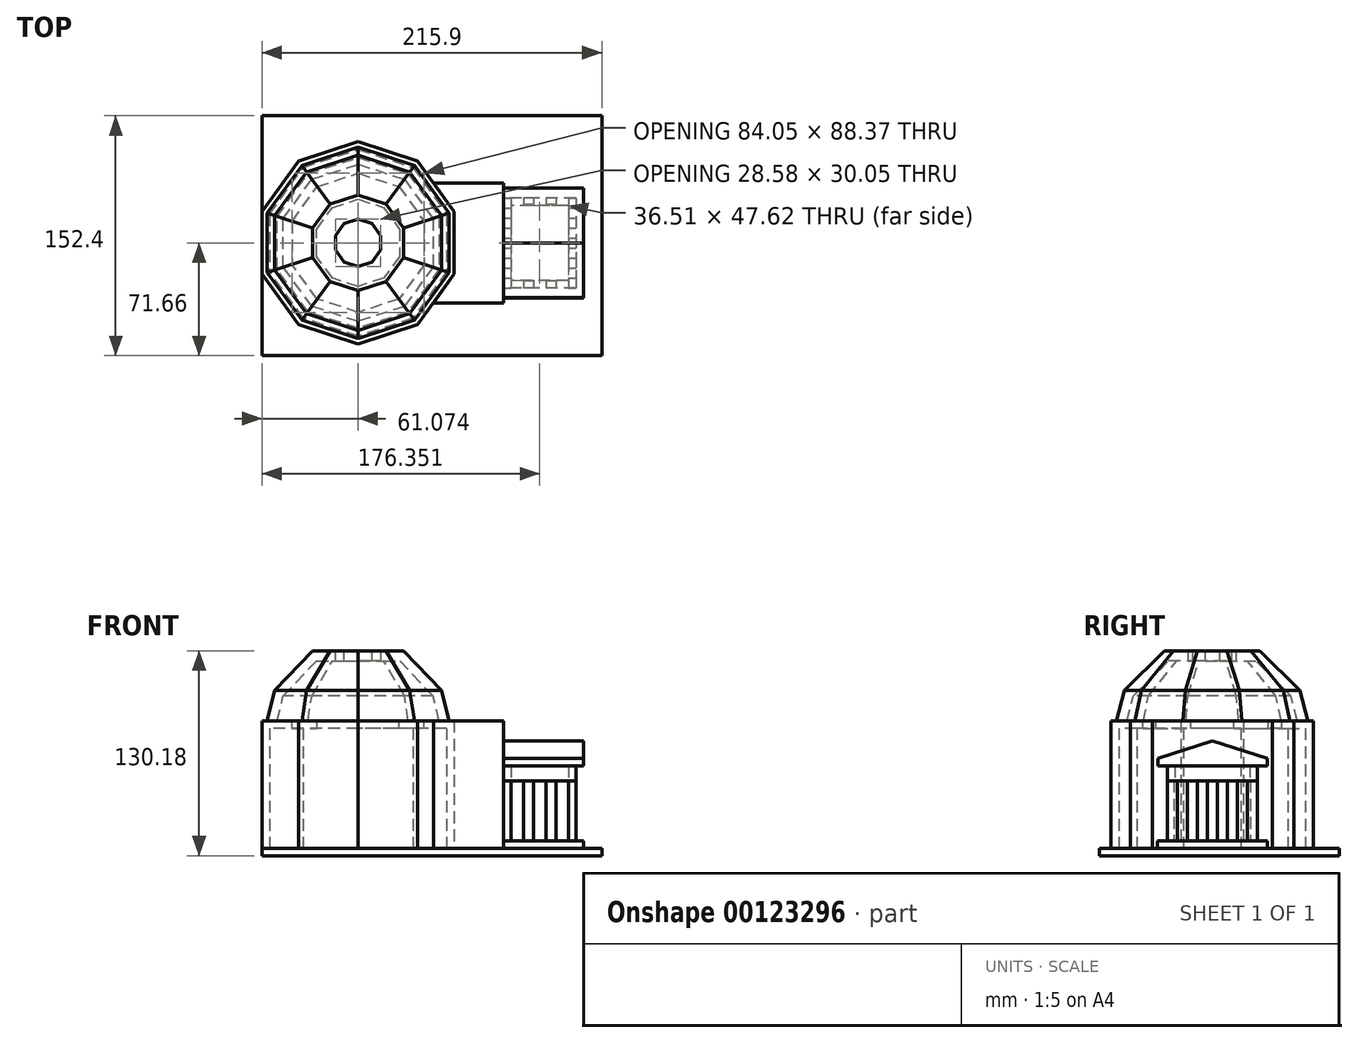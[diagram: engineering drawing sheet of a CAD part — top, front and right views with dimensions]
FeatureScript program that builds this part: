
annotation { "Feature Type Name" : "Feature", "Feature Type Description" : "" }
export const myFeature = defineFeature(function(context is Context, id is Id, definition is map)
    precondition{}
    {
        {
            var Q0;
            Q0=qCreatedBy(makeId("Top.planeOp"),FACE);
            var sketch = newSketch(context, id + "F0", { "sketchPlane" : qUnion([Q0])});
            skLineSegment(sketch, "E0.bottom", {"start": v(-108.2, 80.74) * mm, "end": v(107.7, 80.74) * mm});
            skLineSegment(sketch, "E0.top", {"start": v(-108.2, -71.66) * mm, "end": v(107.7, -71.66) * mm});
            skLineSegment(sketch, "E0.left", {"start": v(-108.2, 80.74) * mm, "end": v(-108.2, -71.66) * mm});
            skLineSegment(sketch, "E0.right", {"start": v(107.7, 80.74) * mm, "end": v(107.7, -71.66) * mm});
            skPoint(sketch, "E0.middle", {"position": v(-0.26, 4.54) * mm});
            skSolve(sketch);
        }
        {
            var Q0;
            Q0=qSketchRegion(id+"F0",true);
            extrude(context, id + "F1", {"entities" : qUnion([Q0]), "depth" : 4.76 * mm});
        }
        {
            var Q0;
            Q0=makeQuery(id+"F1.opExtrude","CAP_FACE",FACE,{"disambiguationData":[OSD([sQuery(id+"F0.wireOp",EDGE,"E0.bottom"),sQuery(id+"F0.wireOp",EDGE,"E0.top"),sQuery(id+"F0.wireOp",EDGE,"E0.left"),sQuery(id+"F0.wireOp",EDGE,"E0.right")])],"isStart":false});
            var sketch = newSketch(context, id + "F2", { "sketchPlane" : qUnion([Q0])});
            skCircle(sketch, "E1.cCircle", {"center": v(-47.14, 0) * mm, "radius": 61.07 * mm, "construction": true});
            skLineSegment(sketch, "E1.0", {"start": v(-47.14, 64.22) * mm, "end": v(-9.4, 51.95) * mm});
            skLineSegment(sketch, "E1.1", {"start": v(-9.4, 51.95) * mm, "end": v(13.94, 19.84) * mm});
            skLineSegment(sketch, "E1.2", {"start": v(13.94, 19.84) * mm, "end": v(13.94, -19.84) * mm});
            skLineSegment(sketch, "E1.3", {"start": v(13.94, -19.84) * mm, "end": v(-9.4, -51.95) * mm});
            skLineSegment(sketch, "E1.4", {"start": v(-9.4, -51.95) * mm, "end": v(-47.14, -64.22) * mm});
            skLineSegment(sketch, "E1.5", {"start": v(-47.14, -64.22) * mm, "end": v(-84.88, -51.95) * mm});
            skLineSegment(sketch, "E1.6", {"start": v(-84.88, -51.95) * mm, "end": v(-108.2, -19.84) * mm});
            skLineSegment(sketch, "E1.7", {"start": v(-108.2, -19.84) * mm, "end": v(-108.2, 19.84) * mm});
            skLineSegment(sketch, "E1.8", {"start": v(-108.2, 19.84) * mm, "end": v(-84.88, 51.95) * mm});
            skLineSegment(sketch, "E1.9", {"start": v(-84.88, 51.95) * mm, "end": v(-47.14, 64.22) * mm});
            skPoint(sketch, "E1.0.midPoint", {"position": v(-28.26, 58.08) * mm});
            skLineSegment(sketch, "E2", {"start": v(45.12, 0) * mm, "end": v(45.12, 38.1) * mm});
            skPoint(sketch, "E2.startSnap0", {"position": v(13.94, 0) * mm});
            skLineSegment(sketch, "E3", {"start": v(45.12, 0) * mm, "end": v(45.12, -38.1) * mm});
            skLineSegment(sketch, "E4", {"start": v(45.12, 38.1) * mm, "end": v(0.67, 38.1) * mm});
            skLineSegment(sketch, "E5", {"start": v(45.12, -38.1) * mm, "end": v(0.67, -38.1) * mm});
            skSolve(sketch);
        }
        {
            var Q0;
            {var subQ2=sQuery(id+"F2.wireOp",EDGE,"E1.0");Q0=makeQuery(id+"F2.imprint","IMPRINT",FACE,{"disambiguationData":[TD([[makeQuery(id+"F2.imprint","IMPRINT",EDGE,{"derivedFrom":subQ2}),-1.0]])]});}
            extrude(context, id + "F3", {"entities" : qUnion([Q0]), "depth" : 80.96 * mm});
        }
        {
            var Q0;
            Q0=makeQuery(id+"F3.opExtrude","CAP_FACE",FACE,{"disambiguationData":[OSD([sQuery(id+"F2.wireOp",EDGE,"E1.0"),sQuery(id+"F2.wireOp",EDGE,"E1.1"),sQuery(id+"F2.wireOp",EDGE,"E1.2"),sQuery(id+"F2.wireOp",EDGE,"E1.3"),sQuery(id+"F2.wireOp",EDGE,"E1.4"),sQuery(id+"F2.wireOp",EDGE,"E1.5"),sQuery(id+"F2.wireOp",EDGE,"E1.6"),sQuery(id+"F2.wireOp",EDGE,"E1.7"),sQuery(id+"F2.wireOp",EDGE,"E1.8"),sQuery(id+"F2.wireOp",EDGE,"E1.9")])],"isStart":true});
            shell(context, id + "F4", {"entities" : qUnion([Q0]), "thickness" : 4.76 * mm});
        }
        {
            var Q0;
            Q0=makeQuery(id+"F3.opExtrude","CAP_FACE",FACE,{"disambiguationData":[OSD([sQuery(id+"F2.wireOp",EDGE,"E1.0"),sQuery(id+"F2.wireOp",EDGE,"E1.1"),sQuery(id+"F2.wireOp",EDGE,"E1.2"),sQuery(id+"F2.wireOp",EDGE,"E1.3"),sQuery(id+"F2.wireOp",EDGE,"E1.4"),sQuery(id+"F2.wireOp",EDGE,"E1.5"),sQuery(id+"F2.wireOp",EDGE,"E1.6"),sQuery(id+"F2.wireOp",EDGE,"E1.7"),sQuery(id+"F2.wireOp",EDGE,"E1.8"),sQuery(id+"F2.wireOp",EDGE,"E1.9")])],"isStart":false});
            var sketch = newSketch(context, id + "F5", { "sketchPlane" : qUnion([Q0])});
            skLineSegment(sketch, "E6.0", {"start": v(-89.16, 13.65) * mm, "end": v(-73.1, 35.75) * mm});
            skLineSegment(sketch, "E6.1", {"start": v(-73.1, 35.75) * mm, "end": v(-47.14, 44.19) * mm});
            skLineSegment(sketch, "E6.2", {"start": v(-89.16, 13.65) * mm, "end": v(-89.16, -13.65) * mm});
            skLineSegment(sketch, "E6.3", {"start": v(-47.14, 44.19) * mm, "end": v(-21.16, 35.75) * mm});
            skLineSegment(sketch, "E6.4", {"start": v(-21.16, 35.75) * mm, "end": v(-5.11, 13.65) * mm});
            skLineSegment(sketch, "E6.5", {"start": v(-5.11, 13.65) * mm, "end": v(-5.11, -13.65) * mm});
            skLineSegment(sketch, "E6.6", {"start": v(-73.1, -35.75) * mm, "end": v(-89.16, -13.65) * mm});
            skLineSegment(sketch, "E6.7", {"start": v(-47.14, -44.19) * mm, "end": v(-73.1, -35.75) * mm});
            skLineSegment(sketch, "E6.8", {"start": v(-21.16, -35.75) * mm, "end": v(-47.14, -44.19) * mm});
            skLineSegment(sketch, "E6.9", {"start": v(-5.11, -13.65) * mm, "end": v(-21.16, -35.75) * mm});
            skSolve(sketch);
        }
        {
            var Q0;
            Q0=qSketchRegion(id+"F5",true);
            extrude(context, id + "F6", {"entities" : qUnion([Q0]), "operationType" : NewBodyOperationType.REMOVE, "oppositeDirection" : true, "depth" : 25.4 * mm});
        }
        {
            var Q0;
            {var subQ1=sQuery(id+"F2.wireOp",EDGE,"E1.2");Q0=makeQuery(id+"F2.imprint","IMPRINT",FACE,{"disambiguationData":[TD([[makeQuery(id+"F2.imprint","IMPRINT",EDGE,{"derivedFrom":subQ1}),1.0]])]});}
            var Q1;
            Q1=makeQuery(id+"F3.opExtrude","CAP_FACE",FACE,{"disambiguationData":[OSD([sQuery(id+"F2.wireOp",EDGE,"E1.0"),sQuery(id+"F2.wireOp",EDGE,"E1.1"),sQuery(id+"F2.wireOp",EDGE,"E1.2"),sQuery(id+"F2.wireOp",EDGE,"E1.3"),sQuery(id+"F2.wireOp",EDGE,"E1.4"),sQuery(id+"F2.wireOp",EDGE,"E1.5"),sQuery(id+"F2.wireOp",EDGE,"E1.6"),sQuery(id+"F2.wireOp",EDGE,"E1.7"),sQuery(id+"F2.wireOp",EDGE,"E1.8"),sQuery(id+"F2.wireOp",EDGE,"E1.9")])],"isStart":false});
            extrude(context, id + "F7", {"entities" : qUnion([Q0]), "endBound" : BoundingType.UP_TO_SURFACE, "endBoundEntityFace" : qUnion([Q1]), "depth" : 25.4 * mm});
        }
        {
            var Q0;
            {var subQ2=sQuery(id+"F2.wireOp",EDGE,"E1.0");Q0=makeQuery(id+"F2.imprint","IMPRINT",FACE,{"disambiguationData":[TD([[makeQuery(id+"F2.imprint","IMPRINT",EDGE,{"derivedFrom":subQ2}),1.0]])]});}
            var sketch = newSketch(context, id + "F8", { "sketchPlane" : qUnion([Q0])});
            skLineSegment(sketch, "E7.bottom", {"start": v(45.12, 34.93) * mm, "end": v(95.92, 34.93) * mm});
            skLineSegment(sketch, "E7.top", {"start": v(45.12, -34.92) * mm, "end": v(95.92, -34.92) * mm});
            skLineSegment(sketch, "E7.left", {"start": v(45.12, 34.93) * mm, "end": v(45.12, -34.93) * mm});
            skLineSegment(sketch, "E7.right", {"start": v(95.92, 34.93) * mm, "end": v(95.92, -34.92) * mm});
            skPoint(sketch, "E7.middle", {"position": v(70.52, 0) * mm});
            skSolve(sketch);
        }
        {
            var Q0;
            Q0=qSketchRegion(id+"F8",true);
            extrude(context, id + "F9", {"entities" : qUnion([Q0]), "depth" : 4.76 * mm});
        }
        {
            var Q0;
            Q0=makeQuery(id+"F9.opExtrude","CAP_FACE",FACE,{"disambiguationData":[OSD([sQuery(id+"F8.wireOp",EDGE,"E7.bottom"),sQuery(id+"F8.wireOp",EDGE,"E7.top"),sQuery(id+"F8.wireOp",EDGE,"E7.left"),sQuery(id+"F8.wireOp",EDGE,"E7.right")])],"isStart":false});
            var sketch = newSketch(context, id + "F10", { "sketchPlane" : qUnion([Q0])});
            skLineSegment(sketch, "E8.bottom", {"start": v(86.4, 28.58) * mm, "end": v(91.16, 28.58) * mm});
            skLineSegment(sketch, "E8.top", {"start": v(86.4, 22.23) * mm, "end": v(91.16, 22.23) * mm});
            skLineSegment(sketch, "E8.left", {"start": v(86.4, 28.58) * mm, "end": v(86.4, 22.23) * mm});
            skLineSegment(sketch, "E8.right", {"start": v(91.16, 28.58) * mm, "end": v(91.16, 22.23) * mm});
            skLineSegment(sketch, "E9.0.1.0", {"start": v(86.4, 9.53) * mm, "end": v(91.16, 9.53) * mm});
            skLineSegment(sketch, "E9.0.1.1", {"start": v(86.4, 15.88) * mm, "end": v(91.16, 15.88) * mm});
            skLineSegment(sketch, "E9.0.1.2", {"start": v(86.4, 15.88) * mm, "end": v(86.4, 9.53) * mm});
            skLineSegment(sketch, "E9.0.1.3", {"start": v(91.16, 15.88) * mm, "end": v(91.16, 9.53) * mm});
            skLineSegment(sketch, "E9.0.2.0", {"start": v(86.4, -3.17) * mm, "end": v(91.16, -3.17) * mm});
            skLineSegment(sketch, "E9.0.2.1", {"start": v(86.4, 3.18) * mm, "end": v(91.16, 3.18) * mm});
            skLineSegment(sketch, "E9.0.2.2", {"start": v(86.4, 3.18) * mm, "end": v(86.4, -3.17) * mm});
            skLineSegment(sketch, "E9.0.2.3", {"start": v(91.16, 3.18) * mm, "end": v(91.16, -3.17) * mm});
            skLineSegment(sketch, "E9.0.3.0", {"start": v(86.4, -15.87) * mm, "end": v(91.16, -15.87) * mm});
            skLineSegment(sketch, "E9.0.3.1", {"start": v(86.4, -9.52) * mm, "end": v(91.16, -9.52) * mm});
            skLineSegment(sketch, "E9.0.3.2", {"start": v(86.4, -9.52) * mm, "end": v(86.4, -15.87) * mm});
            skLineSegment(sketch, "E9.0.3.3", {"start": v(91.16, -9.52) * mm, "end": v(91.16, -15.87) * mm});
            skLineSegment(sketch, "E9.0.4.0", {"start": v(86.4, -28.57) * mm, "end": v(91.16, -28.57) * mm});
            skLineSegment(sketch, "E9.0.4.1", {"start": v(86.4, -22.22) * mm, "end": v(91.16, -22.22) * mm});
            skLineSegment(sketch, "E9.0.4.2", {"start": v(86.4, -22.22) * mm, "end": v(86.4, -28.57) * mm});
            skLineSegment(sketch, "E9.0.4.3", {"start": v(91.16, -22.22) * mm, "end": v(91.16, -28.57) * mm});
            skLineSegment(sketch, "E9.direction1", {"start": v(86.4, 22.23) * mm, "end": v(111.8, 22.23) * mm, "construction": true});
            skLineSegment(sketch, "E9.direction2", {"start": v(86.4, 22.23) * mm, "end": v(86.4, 9.53) * mm, "construction": true});
            skLineSegment(sketch, "E10.bottom", {"start": v(78.46, 28.58) * mm, "end": v(72.11, 28.58) * mm});
            skLineSegment(sketch, "E10.top", {"start": v(78.46, 24.34) * mm, "end": v(72.11, 24.34) * mm});
            skLineSegment(sketch, "E10.left", {"start": v(78.46, 28.58) * mm, "end": v(78.46, 24.34) * mm});
            skLineSegment(sketch, "E10.right", {"start": v(72.11, 28.58) * mm, "end": v(72.11, 24.34) * mm});
            skLineSegment(sketch, "E11.bottom", {"start": v(45.12, 28.57) * mm, "end": v(49.89, 28.58) * mm});
            skLineSegment(sketch, "E11.top", {"start": v(45.12, 22.22) * mm, "end": v(49.89, 22.22) * mm});
            skLineSegment(sketch, "E11.left", {"start": v(45.12, 28.57) * mm, "end": v(45.12, 22.22) * mm});
            skLineSegment(sketch, "E11.right", {"start": v(49.89, 28.57) * mm, "end": v(49.89, 22.22) * mm});
            skLineSegment(sketch, "E12.0.1.0", {"start": v(45.12, 9.53) * mm, "end": v(49.89, 9.53) * mm});
            skLineSegment(sketch, "E12.0.1.1", {"start": v(45.12, 15.87) * mm, "end": v(49.89, 15.88) * mm});
            skLineSegment(sketch, "E12.0.1.2", {"start": v(45.12, 15.88) * mm, "end": v(45.12, 9.53) * mm});
            skLineSegment(sketch, "E12.0.1.3", {"start": v(49.89, 15.88) * mm, "end": v(49.89, 9.53) * mm});
            skLineSegment(sketch, "E12.0.2.0", {"start": v(45.12, -3.17) * mm, "end": v(49.89, -3.17) * mm});
            skLineSegment(sketch, "E12.0.2.1", {"start": v(45.12, 3.18) * mm, "end": v(49.89, 3.18) * mm});
            skLineSegment(sketch, "E12.0.2.2", {"start": v(45.12, 3.18) * mm, "end": v(45.12, -3.17) * mm});
            skLineSegment(sketch, "E12.0.2.3", {"start": v(49.89, 3.18) * mm, "end": v(49.89, -3.17) * mm});
            skLineSegment(sketch, "E12.0.3.0", {"start": v(45.12, -15.87) * mm, "end": v(49.89, -15.87) * mm});
            skLineSegment(sketch, "E12.0.3.1", {"start": v(45.12, -9.52) * mm, "end": v(49.89, -9.52) * mm});
            skLineSegment(sketch, "E12.0.3.2", {"start": v(45.12, -9.52) * mm, "end": v(45.12, -15.87) * mm});
            skLineSegment(sketch, "E12.0.3.3", {"start": v(49.89, -9.52) * mm, "end": v(49.89, -15.87) * mm});
            skLineSegment(sketch, "E12.0.4.0", {"start": v(45.12, -28.57) * mm, "end": v(49.89, -28.57) * mm});
            skLineSegment(sketch, "E12.0.4.1", {"start": v(45.12, -22.22) * mm, "end": v(49.89, -22.22) * mm});
            skLineSegment(sketch, "E12.0.4.2", {"start": v(45.12, -22.22) * mm, "end": v(45.12, -28.57) * mm});
            skLineSegment(sketch, "E12.0.4.3", {"start": v(49.89, -22.22) * mm, "end": v(49.89, -28.57) * mm});
            skLineSegment(sketch, "E12.direction1", {"start": v(45.12, 22.22) * mm, "end": v(70.52, 22.22) * mm, "construction": true});
            skLineSegment(sketch, "E12.direction2", {"start": v(45.12, 22.22) * mm, "end": v(45.12, 9.53) * mm, "construction": true});
            skLineSegment(sketch, "E13.bottom", {"start": v(78.46, -24.34) * mm, "end": v(72.11, -24.34) * mm});
            skLineSegment(sketch, "E13.top", {"start": v(78.46, -28.57) * mm, "end": v(72.11, -28.57) * mm});
            skLineSegment(sketch, "E13.left", {"start": v(78.46, -24.34) * mm, "end": v(78.46, -28.57) * mm});
            skLineSegment(sketch, "E13.right", {"start": v(72.11, -24.34) * mm, "end": v(72.11, -28.57) * mm});
            skLineSegment(sketch, "E14.bottom", {"start": v(64.17, -24.34) * mm, "end": v(57.82, -24.34) * mm});
            skLineSegment(sketch, "E14.top", {"start": v(64.17, -28.57) * mm, "end": v(57.82, -28.57) * mm});
            skLineSegment(sketch, "E14.left", {"start": v(64.17, -24.34) * mm, "end": v(64.17, -28.57) * mm});
            skLineSegment(sketch, "E14.right", {"start": v(57.82, -24.34) * mm, "end": v(57.82, -28.57) * mm});
            skLineSegment(sketch, "E15.bottom", {"start": v(64.17, 28.58) * mm, "end": v(57.82, 28.58) * mm});
            skLineSegment(sketch, "E15.top", {"start": v(64.17, 24.34) * mm, "end": v(57.82, 24.34) * mm});
            skLineSegment(sketch, "E15.left", {"start": v(64.17, 28.58) * mm, "end": v(64.17, 24.34) * mm});
            skLineSegment(sketch, "E15.right", {"start": v(57.82, 28.58) * mm, "end": v(57.82, 24.34) * mm});
            skSolve(sketch);
        }
        {
            var Q0;
            Q0=qSketchRegion(id+"F10",true);
            extrude(context, id + "F11", {"entities" : qUnion([Q0]), "depth" : 38.1 * mm});
        }
        {
            var Q0;
            Q0=makeQuery(id+"F11.opExtrude","CAP_FACE",FACE,{"disambiguationData":[OSD([sQuery(id+"F10.wireOp",EDGE,"E12.0.1.0"),sQuery(id+"F10.wireOp",EDGE,"E12.0.1.1"),sQuery(id+"F10.wireOp",EDGE,"E12.0.1.2"),sQuery(id+"F10.wireOp",EDGE,"E12.0.1.3")])],"isStart":false});
            var sketch = newSketch(context, id + "F12", { "sketchPlane" : qUnion([Q0])});
            skLineSegment(sketch, "E16.bottom", {"start": v(91.16, 28.58) * mm, "end": v(45.12, 28.58) * mm});
            skLineSegment(sketch, "E16.top", {"start": v(91.16, -28.57) * mm, "end": v(45.12, -28.57) * mm});
            skLineSegment(sketch, "E16.left", {"start": v(91.16, 28.58) * mm, "end": v(91.16, -28.57) * mm});
            skLineSegment(sketch, "E16.right", {"start": v(45.12, 28.58) * mm, "end": v(45.12, -28.57) * mm});
            skLineSegment(sketch, "E17.0", {"start": v(49.89, 23.81) * mm, "end": v(49.89, -23.81) * mm});
            skLineSegment(sketch, "E17.1", {"start": v(86.4, 23.81) * mm, "end": v(49.89, 23.81) * mm});
            skLineSegment(sketch, "E17.2", {"start": v(86.4, 23.81) * mm, "end": v(86.4, -23.81) * mm});
            skLineSegment(sketch, "E17.3", {"start": v(86.4, -23.81) * mm, "end": v(49.89, -23.81) * mm});
            skSolve(sketch);
        }
        {
            var Q0;
            Q0=qSketchRegion(id+"F12",true);
            extrude(context, id + "F13", {"entities" : qUnion([Q0]), "depth" : 9.52 * mm});
        }
        {
            var Q0;
            Q0=makeQuery(id+"F9.opExtrude","SWEPT_FACE",FACE,{"disambiguationData":[OSD([sQuery(id+"F8.wireOp",EDGE,"E7.right")])]});
            var sketch = newSketch(context, id + "F14", { "sketchPlane" : qUnion([Q0])});
            skLineSegment(sketch, "E18", {"start": v(-28.33, 57.15) * mm, "end": v(-34.68, 57.15) * mm});
            skLineSegment(sketch, "E19", {"start": v(-34.68, 57.15) * mm, "end": v(-34.68, 61.91) * mm});
            skLineSegment(sketch, "E20", {"start": v(-34.68, 61.91) * mm, "end": v(0, 73.02) * mm});
            skLineSegment(sketch, "E21", {"start": v(0, 73.02) * mm, "end": v(34.93, 61.91) * mm});
            skLineSegment(sketch, "E22", {"start": v(34.93, 61.91) * mm, "end": v(34.93, 57.15) * mm});
            skLineSegment(sketch, "E23", {"start": v(34.93, 57.15) * mm, "end": v(28.58, 57.15) * mm});
            skLineSegment(sketch, "E24", {"start": v(-28.33, 57.15) * mm, "end": v(28.58, 57.15) * mm});
            skSolve(sketch);
        }
        {
            var Q0;
            Q0=qSketchRegion(id+"F14",true);
            extrude(context, id + "F15", {"entities" : qUnion([Q0]), "oppositeDirection" : true, "depth" : 50.8 * mm});
        }
        {
            var Q0;
            Q0=makeQuery(id+"F3.opExtrude","SWEPT_FACE",FACE,{"disambiguationData":[OSD([sQuery(id+"F2.wireOp",EDGE,"E1.5")])]});
            var Q1;
            Q1=makeQuery(id+"F3.opExtrude","SWEPT_FACE",FACE,{"disambiguationData":[OSD([sQuery(id+"F2.wireOp",EDGE,"E1.0")])]});
            cPlane(context, id + "F16", {"entities" : qUnion([Q0, Q1]), "cplaneType" : CPlaneType.MID_PLANE, "offset" : 25.4 * mm, "width" : 152.4 * mm, "height" : 152.4 * mm});
        }
        {
            var Q0;
            Q0=qCreatedBy(id+"F16.planeOp",FACE);
            var sketch = newSketch(context, id + "F17", { "sketchPlane" : qUnion([Q0])});
            skPoint(sketch, "E25.0", {"position": v(-44.83, 4.76) * mm});
            skLineSegment(sketch, "E26", {"start": v(-44.83, 4.76) * mm, "end": v(-44.83, 85.72) * mm});
            skLineSegment(sketch, "E27", {"start": v(-44.83, 85.72) * mm, "end": v(9.37, 85.72) * mm});
            skLineSegment(sketch, "E28", {"start": v(9.37, 85.72) * mm, "end": v(5.12, 101.6) * mm});
            skLineSegment(sketch, "E29", {"start": v(5.12, 101.6) * mm, "end": v(-17.1, 123.83) * mm});
            skLineSegment(sketch, "E30", {"start": v(-17.1, 123.83) * mm, "end": v(-29.8, 123.83) * mm});
            skLineSegment(sketch, "E31.0", {"start": v(-14.47, 130.18) * mm, "end": v(-29.8, 130.18) * mm});
            skLineSegment(sketch, "E31.1", {"start": v(10.81, 104.89) * mm, "end": v(-14.47, 130.18) * mm});
            skLineSegment(sketch, "E31.2", {"start": v(15.95, 85.73) * mm, "end": v(10.81, 104.89) * mm});
            skLineSegment(sketch, "E32", {"start": v(9.37, 85.73) * mm, "end": v(15.95, 85.73) * mm});
            skLineSegment(sketch, "E33", {"start": v(-29.8, 130.18) * mm, "end": v(-29.8, 123.83) * mm});
            skSolve(sketch);
        }
        {
            var Q0;
            Q0=makeQuery(id+"F17.imprint","IMPRINT",FACE,{"disambiguationData":[TD([[makeQuery(id+"F17.imprint","IMPRINT",EDGE,{"derivedFrom":sQuery(id+"F17.wireOp",EDGE,"E28")}),-1.0]])]});
            var Q1;
            Q1=sQuery(id+"F5.wireOp",EDGE,"E6.9");
            var Q2;
            Q2=sQuery(id+"F5.wireOp",EDGE,"E6.8");
            var Q3;
            Q3=sQuery(id+"F5.wireOp",EDGE,"E6.7");
            var Q4;
            Q4=sQuery(id+"F5.wireOp",EDGE,"E6.6");
            var Q5;
            Q5=sQuery(id+"F5.wireOp",EDGE,"E6.2");
            var Q6;
            Q6=sQuery(id+"F5.wireOp",EDGE,"E6.0");
            var Q7;
            Q7=sQuery(id+"F5.wireOp",EDGE,"E6.1");
            var Q8;
            Q8=sQuery(id+"F5.wireOp",EDGE,"E6.5");
            var Q9;
            Q9=sQuery(id+"F5.wireOp",EDGE,"E6.4");
            var Q10;
            Q10=sQuery(id+"F5.wireOp",EDGE,"E6.3");
            sweep(context, id + "F18", {"profiles" : qUnion([Q0]), "path" : qUnion([Q1, Q2, Q3, Q4, Q5, Q6, Q7, Q8, Q9, Q10])});
        }
    });
